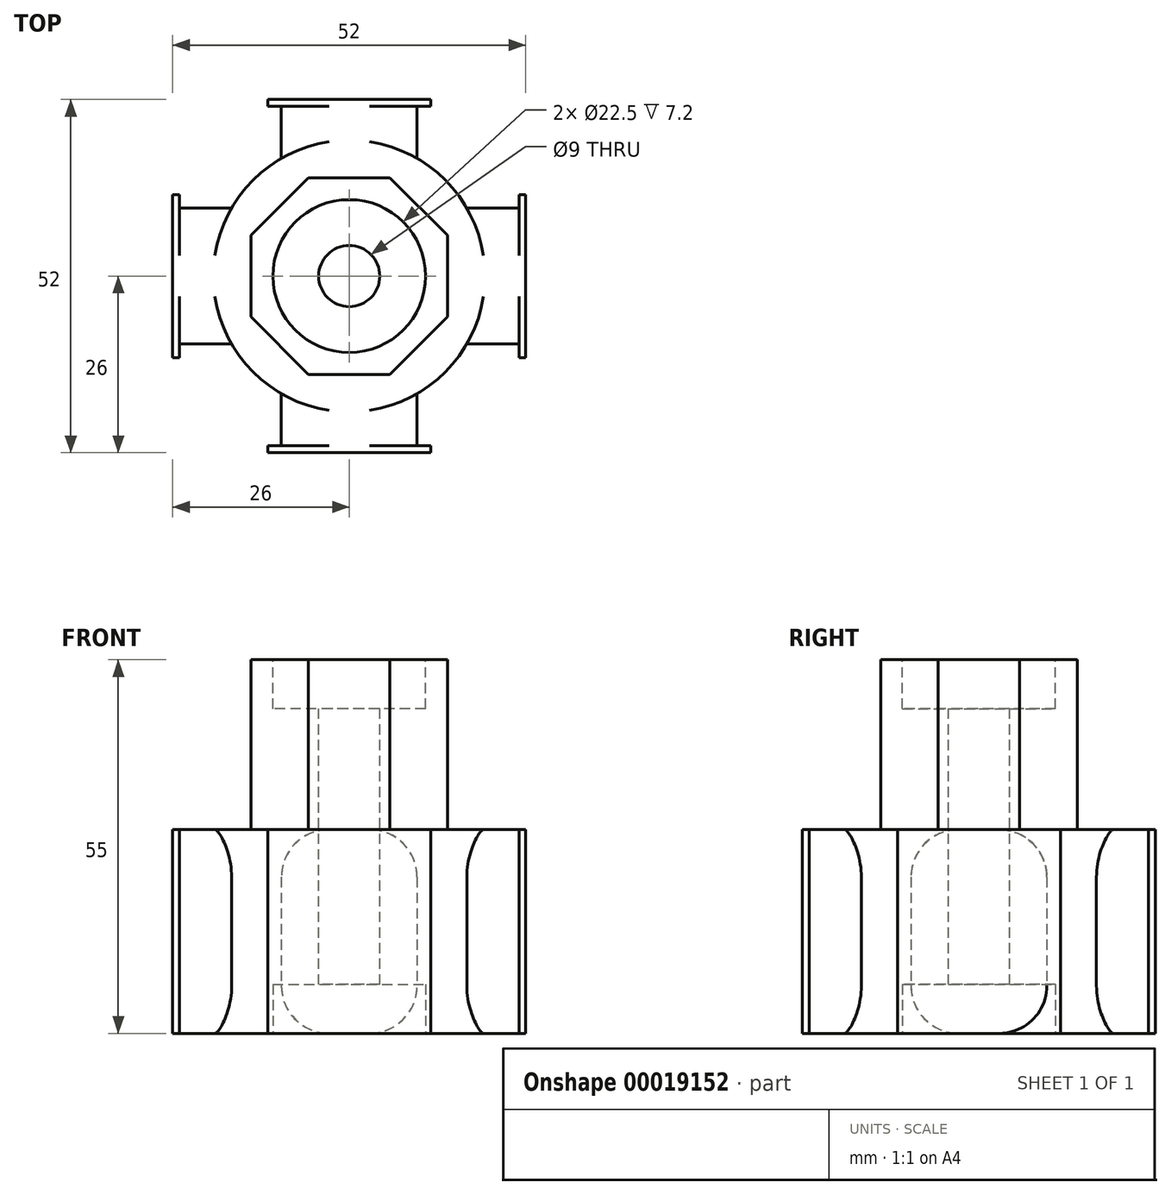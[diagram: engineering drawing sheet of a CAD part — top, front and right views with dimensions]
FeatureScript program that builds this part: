
annotation { "Feature Type Name" : "Feature", "Feature Type Description" : "" }
export const myFeature = defineFeature(function(context is Context, id is Id, definition is map)
    precondition{}
    {
        {
            var Q0;
            Q0=qCreatedBy(makeId("Top.planeOp"),FACE);
            var sketch = newSketch(context, id + "F0", { "sketchPlane" : qUnion([Q0])});
            skCircle(sketch, "E0", {"center": v(0, 0) * mm, "radius": 20 * mm});
            skLineSegment(sketch, "E1.rect.bottom", {"start": v(10, 25) * mm, "end": v(-10, 25) * mm});
            skLineSegment(sketch, "E1.rect.top", {"start": v(10, -25) * mm, "end": v(-10, -25) * mm});
            skLineSegment(sketch, "E1.rect.left", {"start": v(10, 25) * mm, "end": v(10, -25) * mm});
            skLineSegment(sketch, "E1.rect.right", {"start": v(-10, 25) * mm, "end": v(-10, -25) * mm});
            skLineSegment(sketch, "E2.1.0", {"start": v(25, 10) * mm, "end": v(-25, 10) * mm});
            skLineSegment(sketch, "E2.1.1", {"start": v(25, -10) * mm, "end": v(25, 10) * mm});
            skLineSegment(sketch, "E2.1.2", {"start": v(25, -10) * mm, "end": v(-25, -10) * mm});
            skLineSegment(sketch, "E2.1.3", {"start": v(-25, -10) * mm, "end": v(-25, 10) * mm});
            skLineSegment(sketch, "E2.anchor1", {"start": v(0, 0) * mm, "end": v(-10, -25) * mm, "construction": true});
            skLineSegment(sketch, "E2.anchor2", {"start": v(0, 0) * mm, "end": v(-25, 10) * mm, "construction": true});
            skSolve(sketch);
        }
        {
            var Q0;
            {var subQ3=sQuery(id+"F0.wireOp",EDGE,"E1.rect.left");var subQ5=sQuery(id+"F0.wireOp",EDGE,"E0");var subQ6=makeQuery(id+"F0.imprint","INTERSECT",VERTEX,{"disambiguationData":[OD(0.0)],"derivedFrom":[subQ5,subQ3]});Q0=makeQuery(id+"F0.imprint","IMPRINT",FACE,{"disambiguationData":[TD([[makeQuery(id+"F0.imprint","IMPRINT",EDGE,{"disambiguationData":[TD([[subQ6,-1.0]])],"derivedFrom":subQ5}),1.0]])]});}
            var Q1;
            {var subQ3=sQuery(id+"F0.wireOp",EDGE,"E1.rect.bottom");Q1=makeQuery(id+"F0.imprint","IMPRINT",FACE,{"disambiguationData":[TD([[makeQuery(id+"F0.imprint","IMPRINT",EDGE,{"derivedFrom":subQ3}),1.0]])]});}
            var Q2;
            {var subQ1=sQuery(id+"F0.wireOp",EDGE,"E1.rect.right");var subQ3=sQuery(id+"F0.wireOp",EDGE,"E0");var subQ5=makeQuery(id+"F0.imprint","INTERSECT",VERTEX,{"disambiguationData":[OD(0.0)],"derivedFrom":[subQ3,subQ1]});Q2=makeQuery(id+"F0.imprint","IMPRINT",FACE,{"disambiguationData":[TD([[makeQuery(id+"F0.imprint","IMPRINT",EDGE,{"disambiguationData":[TD([[subQ5,-1.0]])],"derivedFrom":subQ3}),1.0]])]});}
            var Q3;
            {var subQ3=sQuery(id+"F0.wireOp",EDGE,"E0");var subQ5=sQuery(id+"F0.wireOp",EDGE,"E2.1.0");var subQ7=makeQuery(id+"F0.imprint","INTERSECT",VERTEX,{"disambiguationData":[OD(1.0)],"derivedFrom":[subQ3,subQ5]});Q3=makeQuery(id+"F0.imprint","IMPRINT",FACE,{"disambiguationData":[TD([[makeQuery(id+"F0.imprint","IMPRINT",EDGE,{"disambiguationData":[TD([[subQ7,-1.0]])],"derivedFrom":subQ3}),1.0]])]});}
            var Q4;
            {var subQ0=sQuery(id+"F0.wireOp",EDGE,"E2.1.3");Q4=makeQuery(id+"F0.imprint","IMPRINT",FACE,{"disambiguationData":[TD([[makeQuery(id+"F0.imprint","IMPRINT",EDGE,{"derivedFrom":subQ0}),-1.0]])]});}
            var Q5;
            {var subQ0=sQuery(id+"F0.wireOp",EDGE,"E2.1.0");var subQ3=sQuery(id+"F0.wireOp",EDGE,"E1.rect.left");var subQ4=makeQuery(id+"F0.imprint","INTERSECT",VERTEX,{"derivedFrom":[subQ3,subQ0]});Q5=makeQuery(id+"F0.imprint","IMPRINT",FACE,{"disambiguationData":[TD([[makeQuery(id+"F0.imprint","IMPRINT",EDGE,{"disambiguationData":[TD([[subQ4,-1.0]])],"derivedFrom":subQ3}),-1.0]])]});}
            var Q6;
            {var subQ0=sQuery(id+"F0.wireOp",EDGE,"E1.rect.right");var subQ3=sQuery(id+"F0.wireOp",EDGE,"E0");var subQ4=makeQuery(id+"F0.imprint","INTERSECT",VERTEX,{"disambiguationData":[OD(1.0)],"derivedFrom":[subQ3,subQ0]});Q6=makeQuery(id+"F0.imprint","IMPRINT",FACE,{"disambiguationData":[TD([[makeQuery(id+"F0.imprint","IMPRINT",EDGE,{"disambiguationData":[TD([[subQ4,-1.0]])],"derivedFrom":subQ3}),1.0]])]});}
            var Q7;
            {var subQ0=sQuery(id+"F0.wireOp",EDGE,"E2.1.2");var subQ3=sQuery(id+"F0.wireOp",EDGE,"E0");var subQ4=makeQuery(id+"F0.imprint","INTERSECT",VERTEX,{"disambiguationData":[OD(0.0)],"derivedFrom":[subQ3,subQ0]});Q7=makeQuery(id+"F0.imprint","IMPRINT",FACE,{"disambiguationData":[TD([[makeQuery(id+"F0.imprint","IMPRINT",EDGE,{"disambiguationData":[TD([[subQ4,-1.0]])],"derivedFrom":subQ3}),1.0]])]});}
            var Q8;
            {var subQ3=sQuery(id+"F0.wireOp",EDGE,"E1.rect.top");Q8=makeQuery(id+"F0.imprint","IMPRINT",FACE,{"disambiguationData":[TD([[makeQuery(id+"F0.imprint","IMPRINT",EDGE,{"derivedFrom":subQ3}),-1.0]])]});}
            var Q9;
            {var subQ1=sQuery(id+"F0.wireOp",EDGE,"E1.rect.left");var subQ3=sQuery(id+"F0.wireOp",EDGE,"E0");var subQ5=makeQuery(id+"F0.imprint","INTERSECT",VERTEX,{"disambiguationData":[OD(1.0)],"derivedFrom":[subQ3,subQ1]});Q9=makeQuery(id+"F0.imprint","IMPRINT",FACE,{"disambiguationData":[TD([[makeQuery(id+"F0.imprint","IMPRINT",EDGE,{"disambiguationData":[TD([[subQ5,-1.0]])],"derivedFrom":subQ3}),1.0]])]});}
            var Q10;
            {var subQ3=sQuery(id+"F0.wireOp",EDGE,"E0");var subQ5=sQuery(id+"F0.wireOp",EDGE,"E2.1.0");var subQ7=makeQuery(id+"F0.imprint","INTERSECT",VERTEX,{"disambiguationData":[OD(0.0)],"derivedFrom":[subQ3,subQ5]});Q10=makeQuery(id+"F0.imprint","IMPRINT",FACE,{"disambiguationData":[TD([[makeQuery(id+"F0.imprint","IMPRINT",EDGE,{"disambiguationData":[TD([[subQ7,1.0]])],"derivedFrom":subQ3}),1.0]])]});}
            var Q11;
            {var subQ3=sQuery(id+"F0.wireOp",EDGE,"E2.1.1");Q11=makeQuery(id+"F0.imprint","IMPRINT",FACE,{"disambiguationData":[TD([[makeQuery(id+"F0.imprint","IMPRINT",EDGE,{"derivedFrom":subQ3}),1.0]])]});}
            var Q12;
            {var subQ1=sQuery(id+"F0.wireOp",EDGE,"E1.rect.left");var subQ3=sQuery(id+"F0.wireOp",EDGE,"E0");var subQ5=makeQuery(id+"F0.imprint","INTERSECT",VERTEX,{"disambiguationData":[OD(0.0)],"derivedFrom":[subQ3,subQ1]});Q12=makeQuery(id+"F0.imprint","IMPRINT",FACE,{"disambiguationData":[TD([[makeQuery(id+"F0.imprint","IMPRINT",EDGE,{"disambiguationData":[TD([[subQ5,1.0]])],"derivedFrom":subQ3}),1.0]])]});}
            extrude(context, id + "F1", {"entities" : qUnion([Q0, Q1, Q2, Q3, Q4, Q5, Q6, Q7, Q8, Q9, Q10, Q11, Q12]), "depth" : 30 * mm});
        }
        {
            var Q0;
            {var subQ0=sQuery(id+"F0.wireOp",EDGE,"E2.1.2");Q0=makeQuery(id+"F1.opExtrude","CAP_EDGE",EDGE,{"disambiguationData":[OSD([subQ0]),TDD([makeQuery(id+"F0.imprint","IMPRINT",EDGE,{"disambiguationData":[TD([[makeQuery(id+"F0.imprint","INTERSECT",VERTEX,{"derivedFrom":[sQuery(id+"F0.wireOp",EDGE,"E2.1.1"),subQ0]}),-1.0]])],"derivedFrom":subQ0})])],"isStart":false});}
            var Q1;
            {var subQ0=sQuery(id+"F0.wireOp",EDGE,"E2.1.0");Q1=makeQuery(id+"F1.opExtrude","CAP_EDGE",EDGE,{"disambiguationData":[OSD([subQ0]),TDD([makeQuery(id+"F0.imprint","IMPRINT",EDGE,{"disambiguationData":[TD([[makeQuery(id+"F0.imprint","INTERSECT",VERTEX,{"derivedFrom":[subQ0,sQuery(id+"F0.wireOp",EDGE,"E2.1.1")]}),-1.0]])],"derivedFrom":subQ0})])],"isStart":false});}
            var Q2;
            {var subQ0=sQuery(id+"F0.wireOp",EDGE,"E2.1.2");Q2=makeQuery(id+"F1.opExtrude","CAP_EDGE",EDGE,{"disambiguationData":[OSD([subQ0]),TDD([makeQuery(id+"F0.imprint","IMPRINT",EDGE,{"disambiguationData":[TD([[makeQuery(id+"F0.imprint","INTERSECT",VERTEX,{"derivedFrom":[sQuery(id+"F0.wireOp",EDGE,"E2.1.1"),subQ0]}),-1.0]])],"derivedFrom":subQ0})])],"isStart":true});}
            var Q3;
            {var subQ0=sQuery(id+"F0.wireOp",EDGE,"E2.1.0");Q3=makeQuery(id+"F1.opExtrude","CAP_EDGE",EDGE,{"disambiguationData":[OSD([subQ0]),TDD([makeQuery(id+"F0.imprint","IMPRINT",EDGE,{"disambiguationData":[TD([[makeQuery(id+"F0.imprint","INTERSECT",VERTEX,{"derivedFrom":[subQ0,sQuery(id+"F0.wireOp",EDGE,"E2.1.1")]}),-1.0]])],"derivedFrom":subQ0})])],"isStart":true});}
            fillet(context, id + "F2", {"entities" : qUnion([Q0, Q1, Q2, Q3]), "radius" : 7 * mm, "tangentPropagation" : true, "allowEdgeOverflow" : false});
        }
        {
            var Q0;
            {var subQ0=sQuery(id+"F0.wireOp",EDGE,"E2.1.0");var subQ1=sQuery(id+"F0.wireOp",EDGE,"E0");var subQ2=sQuery(id+"F0.wireOp",EDGE,"E2.1.1");Q0=makeQuery(id+"F2.opFillet","BLEND_EDGE",EDGE,{"blendedFrom":[makeQuery(id+"F1.opExtrude","CAP_EDGE",EDGE,{"disambiguationData":[OSD([subQ0]),TDD([makeQuery(id+"F0.imprint","IMPRINT",EDGE,{"disambiguationData":[TD([[makeQuery(id+"F0.imprint","INTERSECT",VERTEX,{"derivedFrom":[subQ0,subQ2]}),-1.0]])],"derivedFrom":subQ0})])],"isStart":false}),makeQuery(id+"F1.opExtrude","CAP_FACE",FACE,{"disambiguationData":[OSD([subQ1,sQuery(id+"F0.wireOp",EDGE,"E1.rect.bottom"),sQuery(id+"F0.wireOp",EDGE,"E1.rect.top"),sQuery(id+"F0.wireOp",EDGE,"E1.rect.left"),sQuery(id+"F0.wireOp",EDGE,"E1.rect.right"),subQ0,subQ2,sQuery(id+"F0.wireOp",EDGE,"E2.1.2"),sQuery(id+"F0.wireOp",EDGE,"E2.1.3")])],"isStart":false})],"blendedInto":[makeQuery(id+"F1.opExtrude","CAP_FACE",FACE,{"disambiguationData":[OSD([subQ1,sQuery(id+"F0.wireOp",EDGE,"E1.rect.bottom"),sQuery(id+"F0.wireOp",EDGE,"E1.rect.top"),sQuery(id+"F0.wireOp",EDGE,"E1.rect.left"),sQuery(id+"F0.wireOp",EDGE,"E1.rect.right"),subQ0,subQ2,sQuery(id+"F0.wireOp",EDGE,"E2.1.2"),sQuery(id+"F0.wireOp",EDGE,"E2.1.3")])],"isStart":false})]});}
            var Q1;
            {var subQ0=sQuery(id+"F0.wireOp",EDGE,"E1.rect.left");Q1=makeQuery(id+"F1.opExtrude","CAP_EDGE",EDGE,{"disambiguationData":[OSD([subQ0]),TDD([makeQuery(id+"F0.imprint","IMPRINT",EDGE,{"disambiguationData":[TD([[makeQuery(id+"F0.imprint","INTERSECT",VERTEX,{"derivedFrom":[sQuery(id+"F0.wireOp",EDGE,"E1.rect.bottom"),subQ0]}),-1.0]])],"derivedFrom":subQ0})])],"isStart":false});}
            var Q2;
            {var subQ0=sQuery(id+"F0.wireOp",EDGE,"E1.rect.right");Q2=makeQuery(id+"F1.opExtrude","CAP_EDGE",EDGE,{"disambiguationData":[OSD([subQ0]),TDD([makeQuery(id+"F0.imprint","IMPRINT",EDGE,{"disambiguationData":[TD([[makeQuery(id+"F0.imprint","INTERSECT",VERTEX,{"derivedFrom":[sQuery(id+"F0.wireOp",EDGE,"E1.rect.bottom"),subQ0]}),-1.0]])],"derivedFrom":subQ0})])],"isStart":false});}
            var Q3;
            {var subQ0=sQuery(id+"F0.wireOp",EDGE,"E1.rect.right");Q3=makeQuery(id+"F1.opExtrude","CAP_EDGE",EDGE,{"disambiguationData":[OSD([subQ0]),TDD([makeQuery(id+"F0.imprint","IMPRINT",EDGE,{"disambiguationData":[TD([[makeQuery(id+"F0.imprint","INTERSECT",VERTEX,{"derivedFrom":[sQuery(id+"F0.wireOp",EDGE,"E1.rect.bottom"),subQ0]}),-1.0]])],"derivedFrom":subQ0})])],"isStart":true});}
            var Q4;
            {var subQ0=sQuery(id+"F0.wireOp",EDGE,"E1.rect.left");Q4=makeQuery(id+"F1.opExtrude","CAP_EDGE",EDGE,{"disambiguationData":[OSD([subQ0]),TDD([makeQuery(id+"F0.imprint","IMPRINT",EDGE,{"disambiguationData":[TD([[makeQuery(id+"F0.imprint","INTERSECT",VERTEX,{"derivedFrom":[sQuery(id+"F0.wireOp",EDGE,"E1.rect.bottom"),subQ0]}),-1.0]])],"derivedFrom":subQ0})])],"isStart":true});}
            var Q5;
            {var subQ0=sQuery(id+"F0.wireOp",EDGE,"E2.1.0");Q5=makeQuery(id+"F1.opExtrude","CAP_EDGE",EDGE,{"disambiguationData":[OSD([subQ0]),TDD([makeQuery(id+"F0.imprint","IMPRINT",EDGE,{"disambiguationData":[TD([[makeQuery(id+"F0.imprint","INTERSECT",VERTEX,{"derivedFrom":[subQ0,sQuery(id+"F0.wireOp",EDGE,"E2.1.3")]}),1.0]])],"derivedFrom":subQ0})])],"isStart":true});}
            var Q6;
            {var subQ0=sQuery(id+"F0.wireOp",EDGE,"E2.1.2");Q6=makeQuery(id+"F1.opExtrude","CAP_EDGE",EDGE,{"disambiguationData":[OSD([subQ0]),TDD([makeQuery(id+"F0.imprint","IMPRINT",EDGE,{"disambiguationData":[TD([[makeQuery(id+"F0.imprint","INTERSECT",VERTEX,{"derivedFrom":[subQ0,sQuery(id+"F0.wireOp",EDGE,"E2.1.3")]}),1.0]])],"derivedFrom":subQ0})])],"isStart":true});}
            var Q7;
            {var subQ0=sQuery(id+"F0.wireOp",EDGE,"E1.rect.right");Q7=makeQuery(id+"F1.opExtrude","CAP_EDGE",EDGE,{"disambiguationData":[OSD([subQ0]),TDD([makeQuery(id+"F0.imprint","IMPRINT",EDGE,{"disambiguationData":[TD([[makeQuery(id+"F0.imprint","INTERSECT",VERTEX,{"derivedFrom":[sQuery(id+"F0.wireOp",EDGE,"E1.rect.top"),subQ0]}),1.0]])],"derivedFrom":subQ0})])],"isStart":true});}
            var Q8;
            {var subQ0=sQuery(id+"F0.wireOp",EDGE,"E1.rect.left");Q8=makeQuery(id+"F1.opExtrude","CAP_EDGE",EDGE,{"disambiguationData":[OSD([subQ0]),TDD([makeQuery(id+"F0.imprint","IMPRINT",EDGE,{"disambiguationData":[TD([[makeQuery(id+"F0.imprint","INTERSECT",VERTEX,{"derivedFrom":[sQuery(id+"F0.wireOp",EDGE,"E1.rect.top"),subQ0]}),1.0]])],"derivedFrom":subQ0})])],"isStart":true});}
            var Q9;
            {var subQ0=sQuery(id+"F0.wireOp",EDGE,"E2.1.0");Q9=makeQuery(id+"F1.opExtrude","CAP_EDGE",EDGE,{"disambiguationData":[OSD([subQ0]),TDD([makeQuery(id+"F0.imprint","IMPRINT",EDGE,{"disambiguationData":[TD([[makeQuery(id+"F0.imprint","INTERSECT",VERTEX,{"derivedFrom":[subQ0,sQuery(id+"F0.wireOp",EDGE,"E2.1.3")]}),1.0]])],"derivedFrom":subQ0})])],"isStart":false});}
            var Q10;
            {var subQ0=sQuery(id+"F0.wireOp",EDGE,"E2.1.2");Q10=makeQuery(id+"F1.opExtrude","CAP_EDGE",EDGE,{"disambiguationData":[OSD([subQ0]),TDD([makeQuery(id+"F0.imprint","IMPRINT",EDGE,{"disambiguationData":[TD([[makeQuery(id+"F0.imprint","INTERSECT",VERTEX,{"derivedFrom":[subQ0,sQuery(id+"F0.wireOp",EDGE,"E2.1.3")]}),1.0]])],"derivedFrom":subQ0})])],"isStart":false});}
            var Q11;
            {var subQ0=sQuery(id+"F0.wireOp",EDGE,"E1.rect.right");Q11=makeQuery(id+"F1.opExtrude","CAP_EDGE",EDGE,{"disambiguationData":[OSD([subQ0]),TDD([makeQuery(id+"F0.imprint","IMPRINT",EDGE,{"disambiguationData":[TD([[makeQuery(id+"F0.imprint","INTERSECT",VERTEX,{"derivedFrom":[sQuery(id+"F0.wireOp",EDGE,"E1.rect.top"),subQ0]}),1.0]])],"derivedFrom":subQ0})])],"isStart":false});}
            var Q12;
            {var subQ0=sQuery(id+"F0.wireOp",EDGE,"E1.rect.left");Q12=makeQuery(id+"F1.opExtrude","CAP_EDGE",EDGE,{"disambiguationData":[OSD([subQ0]),TDD([makeQuery(id+"F0.imprint","IMPRINT",EDGE,{"disambiguationData":[TD([[makeQuery(id+"F0.imprint","INTERSECT",VERTEX,{"derivedFrom":[sQuery(id+"F0.wireOp",EDGE,"E1.rect.top"),subQ0]}),1.0]])],"derivedFrom":subQ0})])],"isStart":false});}
            fillet(context, id + "F3", {"entities" : qUnion([Q0, Q1, Q2, Q3, Q4, Q5, Q6, Q7, Q8, Q9, Q10, Q11, Q12]), "radius" : 7 * mm, "tangentPropagation" : true, "allowEdgeOverflow" : false});
        }
        {
            var Q0;
            Q0=makeQuery(id+"F1.opExtrude","CAP_FACE",FACE,{"disambiguationData":[OSD([sQuery(id+"F0.wireOp",EDGE,"E0"),sQuery(id+"F0.wireOp",EDGE,"E1.rect.bottom"),sQuery(id+"F0.wireOp",EDGE,"E1.rect.top"),sQuery(id+"F0.wireOp",EDGE,"E1.rect.left"),sQuery(id+"F0.wireOp",EDGE,"E1.rect.right"),sQuery(id+"F0.wireOp",EDGE,"E2.1.0"),sQuery(id+"F0.wireOp",EDGE,"E2.1.1"),sQuery(id+"F0.wireOp",EDGE,"E2.1.2"),sQuery(id+"F0.wireOp",EDGE,"E2.1.3")])],"isStart":false});
            var sketch = newSketch(context, id + "F4", { "sketchPlane" : qUnion([Q0])});
            skCircle(sketch, "E3.cCircle", {"center": v(0, 0) * mm, "radius": 14.49 * mm, "construction": true});
            skLineSegment(sketch, "E3.0", {"start": v(6, -14.49) * mm, "end": v(-6, -14.49) * mm});
            skLineSegment(sketch, "E3.1", {"start": v(-6, -14.49) * mm, "end": v(-14.49, -6) * mm});
            skLineSegment(sketch, "E3.2", {"start": v(-14.49, -6) * mm, "end": v(-14.49, 6) * mm});
            skLineSegment(sketch, "E3.3", {"start": v(-14.49, 6) * mm, "end": v(-6, 14.49) * mm});
            skLineSegment(sketch, "E3.4", {"start": v(-6, 14.49) * mm, "end": v(6, 14.49) * mm});
            skLineSegment(sketch, "E3.5", {"start": v(6, 14.49) * mm, "end": v(14.49, 6) * mm});
            skLineSegment(sketch, "E3.6", {"start": v(14.49, 6) * mm, "end": v(14.49, -6) * mm});
            skLineSegment(sketch, "E3.7", {"start": v(14.49, -6) * mm, "end": v(6, -14.49) * mm});
            skPoint(sketch, "E3.0.midPoint", {"position": v(0, -14.49) * mm});
            skSolve(sketch);
        }
        {
            var Q0;
            Q0=makeQuery(id+"F4.imprint","IMPRINT",FACE,{"disambiguationData":[TD([[makeQuery(id+"F4.imprint","IMPRINT",EDGE,{"derivedFrom":sQuery(id+"F4.wireOp",EDGE,"E3.0")}),-1.0]])]});
            extrude(context, id + "F5", {"entities" : qUnion([Q0]), "operationType" : NewBodyOperationType.ADD, "depth" : 25 * mm});
        }
        {
            var Q0;
            Q0=makeQuery(id+"F5.opExtrude","CAP_FACE",FACE,{"disambiguationData":[OSD([sQuery(id+"F4.wireOp",EDGE,"E3.0"),sQuery(id+"F4.wireOp",EDGE,"E3.1"),sQuery(id+"F4.wireOp",EDGE,"E3.2"),sQuery(id+"F4.wireOp",EDGE,"E3.3"),sQuery(id+"F4.wireOp",EDGE,"E3.4"),sQuery(id+"F4.wireOp",EDGE,"E3.5"),sQuery(id+"F4.wireOp",EDGE,"E3.6"),sQuery(id+"F4.wireOp",EDGE,"E3.7")])],"isStart":false});
            var sketch = newSketch(context, id + "F6", { "sketchPlane" : qUnion([Q0])});
            skCircle(sketch, "E4", {"center": v(0, 0) * mm, "radius": 11.25 * mm});
            skSolve(sketch);
        }
        {
            var Q0;
            Q0=makeQuery(id+"F6.imprint","IMPRINT",FACE,{"disambiguationData":[TD([[makeQuery(id+"F6.imprint","IMPRINT",EDGE,{"derivedFrom":sQuery(id+"F6.wireOp",EDGE,"E4")}),1.0]])]});
            extrude(context, id + "F7", {"entities" : qUnion([Q0]), "operationType" : NewBodyOperationType.REMOVE, "oppositeDirection" : true, "depth" : 7.2 * mm});
        }
        {
            var Q0;
            Q0=makeQuery(id+"F7.boolean.opBoolean","COPY",FACE,{"derivedFrom":makeQuery(id+"F7.opExtrude","CAP_FACE",FACE,{"disambiguationData":[OSD([sQuery(id+"F6.wireOp",EDGE,"E4")])],"isStart":false})});
            var sketch = newSketch(context, id + "F8", { "sketchPlane" : qUnion([Q0])});
            skCircle(sketch, "E5", {"center": v(0, 0) * mm, "radius": 4.5 * mm});
            skSolve(sketch);
        }
        {
            var Q0;
            Q0=makeQuery(id+"F8.imprint","IMPRINT",FACE,{"disambiguationData":[TD([[makeQuery(id+"F8.imprint","IMPRINT",EDGE,{"derivedFrom":sQuery(id+"F8.wireOp",EDGE,"E5")}),1.0]])]});
            extrude(context, id + "F9", {"entities" : qUnion([Q0]), "operationType" : NewBodyOperationType.REMOVE, "endBound" : BoundingType.THROUGH_ALL, "oppositeDirection" : true, "depth" : 25 * mm});
        }
        {
            var Q0;
            Q0=makeQuery(id+"F1.opExtrude","CAP_FACE",FACE,{"disambiguationData":[OSD([sQuery(id+"F0.wireOp",EDGE,"E0"),sQuery(id+"F0.wireOp",EDGE,"E1.rect.bottom"),sQuery(id+"F0.wireOp",EDGE,"E1.rect.top"),sQuery(id+"F0.wireOp",EDGE,"E1.rect.left"),sQuery(id+"F0.wireOp",EDGE,"E1.rect.right"),sQuery(id+"F0.wireOp",EDGE,"E2.1.0"),sQuery(id+"F0.wireOp",EDGE,"E2.1.1"),sQuery(id+"F0.wireOp",EDGE,"E2.1.2"),sQuery(id+"F0.wireOp",EDGE,"E2.1.3")])],"isStart":true});
            var sketch = newSketch(context, id + "F10", { "sketchPlane" : qUnion([Q0])});
            skCircle(sketch, "E6", {"center": v(0, 0) * mm, "radius": 11.25 * mm});
            skSolve(sketch);
        }
        {
            var Q0;
            Q0=makeQuery(id+"F10.imprint","IMPRINT",FACE,{"disambiguationData":[TD([[makeQuery(id+"F10.imprint","IMPRINT",EDGE,{"derivedFrom":sQuery(id+"F10.wireOp",EDGE,"E6")}),1.0]])]});
            extrude(context, id + "F11", {"entities" : qUnion([Q0]), "operationType" : NewBodyOperationType.REMOVE, "oppositeDirection" : true, "depth" : 7.2 * mm});
        }
        {
            var Q0;
            Q0=makeQuery(id+"F1.opExtrude","CAP_FACE",FACE,{"disambiguationData":[OSD([sQuery(id+"F0.wireOp",EDGE,"E0"),sQuery(id+"F0.wireOp",EDGE,"E1.rect.bottom"),sQuery(id+"F0.wireOp",EDGE,"E1.rect.top"),sQuery(id+"F0.wireOp",EDGE,"E1.rect.left"),sQuery(id+"F0.wireOp",EDGE,"E1.rect.right"),sQuery(id+"F0.wireOp",EDGE,"E2.1.0"),sQuery(id+"F0.wireOp",EDGE,"E2.1.1"),sQuery(id+"F0.wireOp",EDGE,"E2.1.2"),sQuery(id+"F0.wireOp",EDGE,"E2.1.3")])],"isStart":true});
            var sketch = newSketch(context, id + "F12", { "sketchPlane" : qUnion([Q0])});
            skLineSegment(sketch, "E7.0", {"start": v(-10, 25) * mm, "end": v(-3, 25) * mm});
            skLineSegment(sketch, "E8.0", {"start": v(3, 25) * mm, "end": v(10, 25) * mm});
            skLineSegment(sketch, "E9.bottom", {"start": v(-12, 25) * mm, "end": v(12, 25) * mm});
            skLineSegment(sketch, "E9.top", {"start": v(-12, 26) * mm, "end": v(12, 26) * mm});
            skLineSegment(sketch, "E9.left", {"start": v(-12, 25) * mm, "end": v(-12, 26) * mm});
            skLineSegment(sketch, "E9.right", {"start": v(12, 25) * mm, "end": v(12, 26) * mm});
            skLineSegment(sketch, "E10.1.0", {"start": v(-26, -12) * mm, "end": v(-26, 12) * mm});
            skLineSegment(sketch, "E10.1.1", {"start": v(-25, -12) * mm, "end": v(-25, 12) * mm});
            skLineSegment(sketch, "E10.1.2", {"start": v(-25, -12) * mm, "end": v(-26, -12) * mm});
            skLineSegment(sketch, "E10.1.3", {"start": v(-25, 12) * mm, "end": v(-26, 12) * mm});
            skLineSegment(sketch, "E10.2.0", {"start": v(12, -26) * mm, "end": v(-12, -26) * mm});
            skLineSegment(sketch, "E10.2.1", {"start": v(12, -25) * mm, "end": v(-12, -25) * mm});
            skLineSegment(sketch, "E10.2.2", {"start": v(12, -25) * mm, "end": v(12, -26) * mm});
            skLineSegment(sketch, "E10.2.3", {"start": v(-12, -25) * mm, "end": v(-12, -26) * mm});
            skLineSegment(sketch, "E10.3.0", {"start": v(26, 12) * mm, "end": v(26, -12) * mm});
            skLineSegment(sketch, "E10.3.1", {"start": v(25, 12) * mm, "end": v(25, -12) * mm});
            skLineSegment(sketch, "E10.3.2", {"start": v(25, 12) * mm, "end": v(26, 12) * mm});
            skLineSegment(sketch, "E10.3.3", {"start": v(25, -12) * mm, "end": v(26, -12) * mm});
            skPoint(sketch, "E10.center", {"position": v(0, 0) * mm});
            skSolve(sketch);
        }
        {
            var Q0;
            Q0=makeQuery(id+"F12.imprint","IMPRINT",FACE,{"disambiguationData":[TD([[makeQuery(id+"F12.imprint","IMPRINT",EDGE,{"derivedFrom":sQuery(id+"F12.wireOp",EDGE,"E9.top")}),-1.0]])]});
            var Q1;
            Q1=makeQuery(id+"F12.imprint","IMPRINT",FACE,{"disambiguationData":[TD([[makeQuery(id+"F12.imprint","IMPRINT",EDGE,{"derivedFrom":sQuery(id+"F12.wireOp",EDGE,"E10.1.0")}),-1.0]])]});
            var Q2;
            Q2=makeQuery(id+"F12.imprint","IMPRINT",FACE,{"disambiguationData":[TD([[makeQuery(id+"F12.imprint","IMPRINT",EDGE,{"derivedFrom":sQuery(id+"F12.wireOp",EDGE,"E10.3.0")}),-1.0]])]});
            var Q3;
            Q3=makeQuery(id+"F12.imprint","IMPRINT",FACE,{"disambiguationData":[TD([[makeQuery(id+"F12.imprint","IMPRINT",EDGE,{"derivedFrom":sQuery(id+"F12.wireOp",EDGE,"E10.2.0")}),-1.0]])]});
            var Q4;
            Q4=makeQuery(id+"F1.opExtrude","CAP_FACE",FACE,{"disambiguationData":[OSD([sQuery(id+"F0.wireOp",EDGE,"E0"),sQuery(id+"F0.wireOp",EDGE,"E1.rect.bottom"),sQuery(id+"F0.wireOp",EDGE,"E1.rect.top"),sQuery(id+"F0.wireOp",EDGE,"E1.rect.left"),sQuery(id+"F0.wireOp",EDGE,"E1.rect.right"),sQuery(id+"F0.wireOp",EDGE,"E2.1.0"),sQuery(id+"F0.wireOp",EDGE,"E2.1.1"),sQuery(id+"F0.wireOp",EDGE,"E2.1.2"),sQuery(id+"F0.wireOp",EDGE,"E2.1.3")])],"isStart":false});
            extrude(context, id + "F13", {"entities" : qUnion([Q0, Q1, Q2, Q3]), "operationType" : NewBodyOperationType.ADD, "endBound" : BoundingType.UP_TO_SURFACE, "oppositeDirection" : true, "endBoundEntityFace" : qUnion([Q4]), "depth" : 25 * mm});
        }
    });
